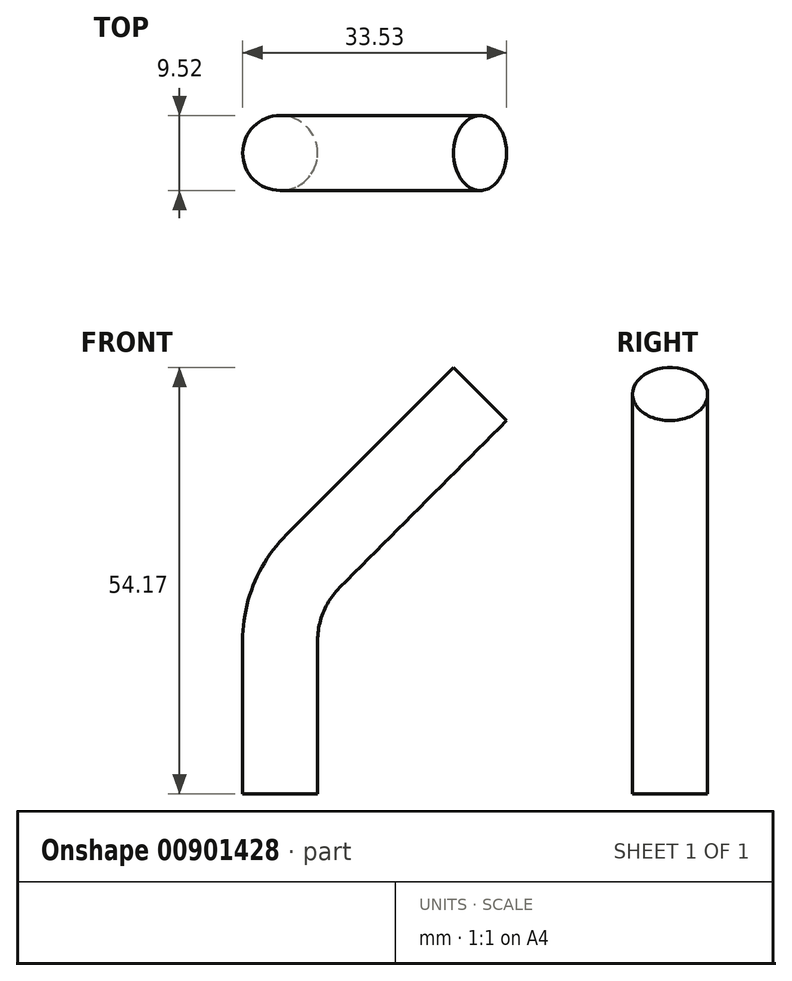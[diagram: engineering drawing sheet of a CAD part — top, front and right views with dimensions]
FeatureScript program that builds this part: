
annotation { "Feature Type Name" : "Feature", "Feature Type Description" : "" }
export const myFeature = defineFeature(function(context is Context, id is Id, definition is map)
    precondition{}
    {
        {
            var Q0;
            Q0=qCreatedBy(makeId("Front.planeOp"),FACE);
            var sketch = newSketch(context, id + "F0", { "sketchPlane" : qUnion([Q0])});
            skLineSegment(sketch, "E0", {"start": v(0, 0) * mm, "end": v(0, 19.48) * mm});
            skLineSegment(sketch, "E1", {"start": v(4.18, 29.58) * mm, "end": v(25.4, 50.8) * mm});
            skPoint(sketch, "E2.visualSharp", {"position": v(0, 25.4) * mm});
            skArc(sketch, "E2.filletArc", {"start": v(4.18, 29.58) * mm, "mid": v(1.09, 24.95) * mm, "end": v(0, 19.48) * mm});
            skSolve(sketch);
        }
        {
            var Q0;
            Q0=qCreatedBy(makeId("Top.planeOp"),FACE);
            var sketch = newSketch(context, id + "F1", { "sketchPlane" : qUnion([Q0])});
            skCircle(sketch, "E3", {"center": v(0, 0) * mm, "radius": 4.76 * mm});
            skSolve(sketch);
        }
        {
            var Q0;
            Q0=makeQuery(id+"F1.imprint","IMPRINT",FACE,{"disambiguationData":[TD([[makeQuery(id+"F1.imprint","IMPRINT",EDGE,{"derivedFrom":sQuery(id+"F1.wireOp",EDGE,"E3")}),1.0]])]});
            var Q1;
            Q1=sQuery(id+"F0.wireOp",EDGE,"E0");
            var Q2;
            Q2=sQuery(id+"F0.wireOp",EDGE,"E2.filletArc");
            var Q3;
            Q3=sQuery(id+"F0.wireOp",EDGE,"E1");
            sweep(context, id + "F2", {"profiles" : qUnion([Q0]), "path" : qUnion([Q1, Q2, Q3])});
        }
    });
